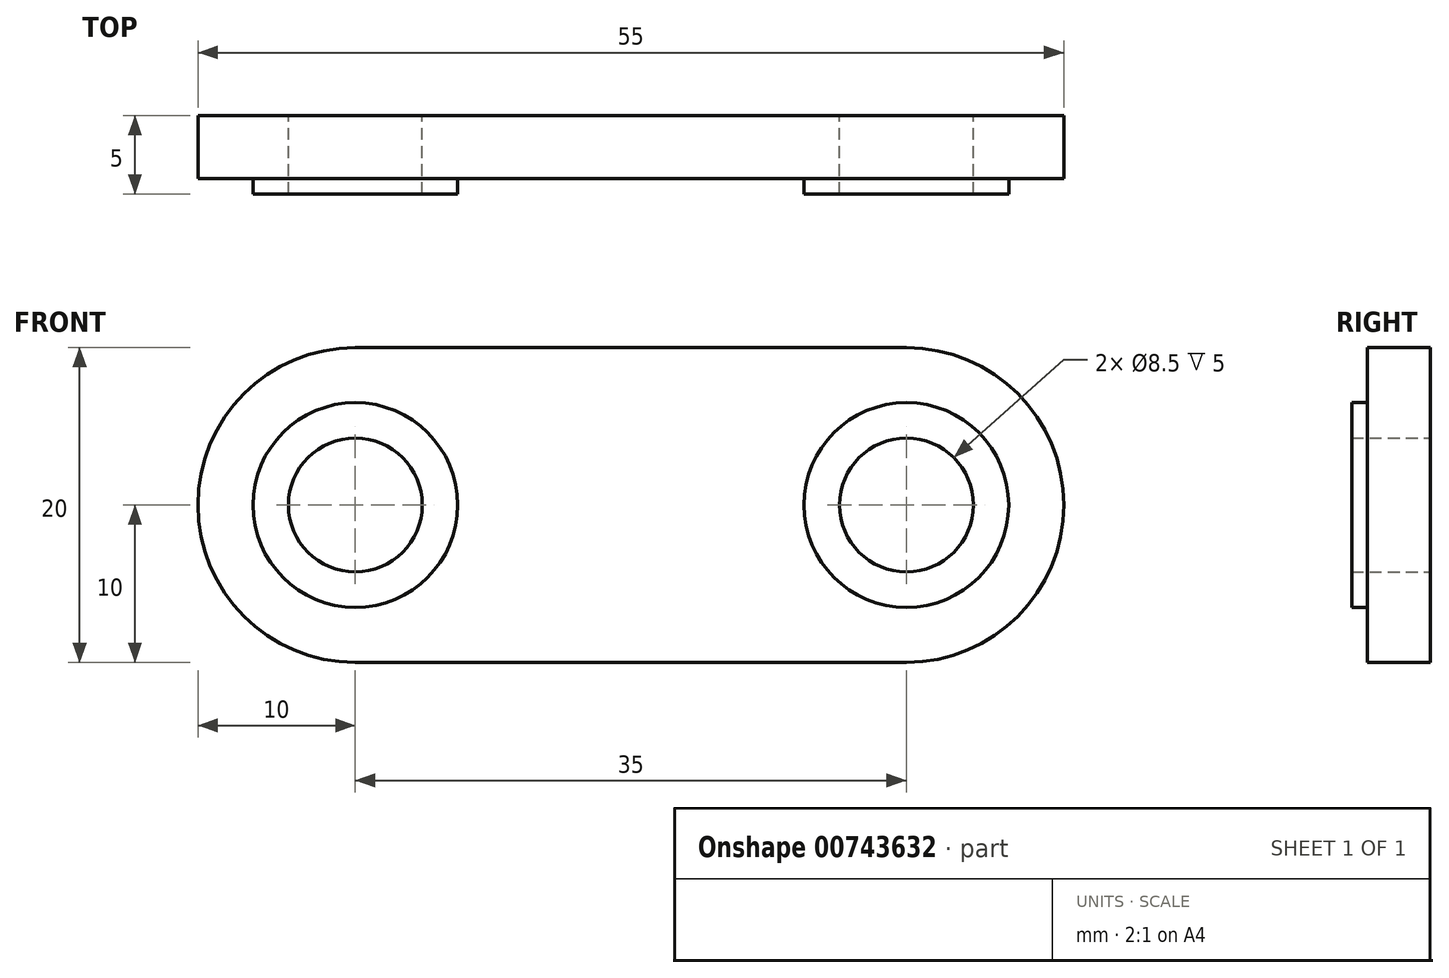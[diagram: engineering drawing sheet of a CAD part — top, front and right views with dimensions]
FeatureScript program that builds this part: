
annotation { "Feature Type Name" : "Feature", "Feature Type Description" : "" }
export const myFeature = defineFeature(function(context is Context, id is Id, definition is map)
    precondition{}
    {
        {
            var Q0;
            Q0=qCreatedBy(makeId("Front.planeOp"),FACE);
            var sketch = newSketch(context, id + "F0", { "sketchPlane" : qUnion([Q0])});
            skCircle(sketch, "E0", {"center": v(-17.5, 0) * mm, "radius": 4.25 * mm});
            skCircle(sketch, "E1", {"center": v(17.5, 0) * mm, "radius": 4.25 * mm});
            skCircle(sketch, "E2", {"center": v(-17.5, 0) * mm, "radius": 10 * mm});
            skCircle(sketch, "E3", {"center": v(17.5, 0) * mm, "radius": 10 * mm});
            skLineSegment(sketch, "E4", {"start": v(-17.5, -10) * mm, "end": v(17.5, -10) * mm});
            skLineSegment(sketch, "E5", {"start": v(-17.5, 10) * mm, "end": v(17.5, 10) * mm});
            skCircle(sketch, "E6", {"center": v(-17.5, 0) * mm, "radius": 6.5 * mm});
            skCircle(sketch, "E7", {"center": v(17.5, 0) * mm, "radius": 6.5 * mm});
            skSolve(sketch);
        }
        {
            var Q0;
            Q0 = qSketchRegion(id + "F0", true);
            var Q1;
            Q1=makeQuery(id+"F0.imprint","IMPRINT",FACE,{"disambiguationData":[TD([[makeQuery(id+"F0.imprint","IMPRINT",EDGE,{"derivedFrom":sQuery(id+"F0.wireOp",EDGE,"E0")}),-1.0]])]});
            var Q2;
            Q2=makeQuery(id+"F0.imprint","IMPRINT",FACE,{"disambiguationData":[TD([[makeQuery(id+"F0.imprint","IMPRINT",EDGE,{"derivedFrom":sQuery(id+"F0.wireOp",EDGE,"E1")}),-1.0]])]});
            extrude(context, id + "F1", {"entities" : qUnion([Q0, Q1, Q2]), "depth" : 4 * mm, "offsetDistance" : 25 * mm});
        }
        {
            var Q0;
            Q0=makeQuery(id+"F0.imprint","IMPRINT",FACE,{"disambiguationData":[TD([[makeQuery(id+"F0.imprint","IMPRINT",EDGE,{"derivedFrom":sQuery(id+"F0.wireOp",EDGE,"E1")}),-1.0]])]});
            var Q1;
            Q1=makeQuery(id+"F0.imprint","IMPRINT",FACE,{"disambiguationData":[TD([[makeQuery(id+"F0.imprint","IMPRINT",EDGE,{"derivedFrom":sQuery(id+"F0.wireOp",EDGE,"E0")}),-1.0]])]});
            extrude(context, id + "F2", {"entities" : qUnion([Q0, Q1]), "operationType" : NewBodyOperationType.ADD, "surfaceOperationType" : NewSurfaceOperationType.ADD, "depth" : 5 * mm, "offsetDistance" : 25 * mm});
        }
    });
